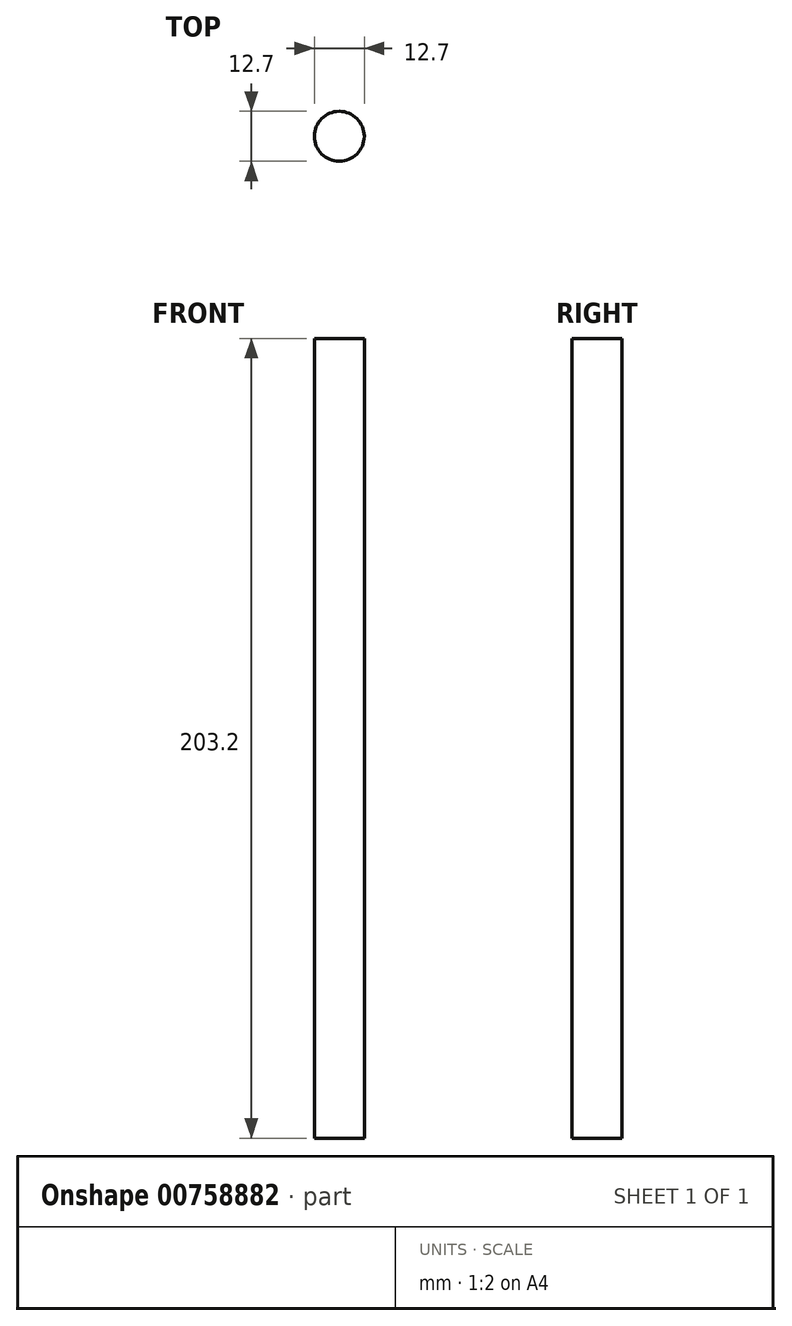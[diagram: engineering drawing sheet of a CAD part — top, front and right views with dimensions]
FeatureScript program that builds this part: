
annotation { "Feature Type Name" : "Feature", "Feature Type Description" : "" }
export const myFeature = defineFeature(function(context is Context, id is Id, definition is map)
    precondition{}
    {
        {
            var Q0;
            Q0=qCreatedBy(makeId("Top.planeOp"),FACE);
            var sketch = newSketch(context, id + "F0", { "sketchPlane" : qUnion([Q0])});
            skCircle(sketch, "E0", {"center": v(0, 0) * mm, "radius": 6.35 * mm});
            skSolve(sketch);
        }
        {
            var Q0;
            Q0 = qSketchRegion(id + "F0", true);
            extrude(context, id + "F1", {"entities" : qUnion([Q0]), "depth" : 203.2 * mm, "offsetDistance" : 25.4 * mm});
        }
    });
